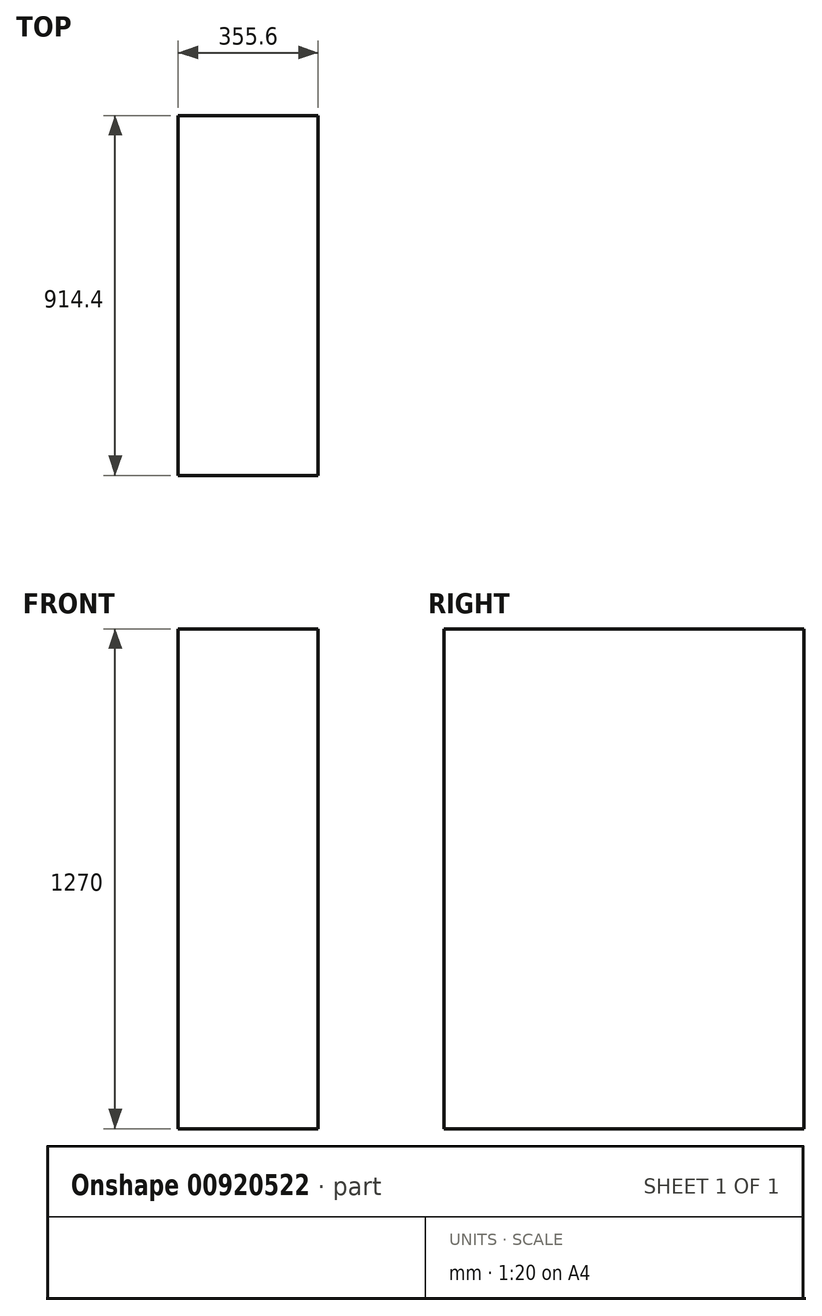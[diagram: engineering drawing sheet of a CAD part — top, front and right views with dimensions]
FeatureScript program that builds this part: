
annotation { "Feature Type Name" : "Feature", "Feature Type Description" : "" }
export const myFeature = defineFeature(function(context is Context, id is Id, definition is map)
    precondition{}
    {
        {
            var Q0;
            Q0=qCreatedBy(makeId("Top.planeOp"),FACE);
            var sketch = newSketch(context, id + "F0", { "sketchPlane" : qUnion([Q0])});
            skLineSegment(sketch, "E0.bottom", {"start": v(177.8, -457.2) * mm, "end": v(-177.8, -457.2) * mm});
            skLineSegment(sketch, "E0.top", {"start": v(177.8, 457.2) * mm, "end": v(-177.8, 457.2) * mm});
            skLineSegment(sketch, "E0.left", {"start": v(177.8, -457.2) * mm, "end": v(177.8, 457.2) * mm});
            skLineSegment(sketch, "E0.right", {"start": v(-177.8, -457.2) * mm, "end": v(-177.8, 457.2) * mm});
            skPoint(sketch, "E0.middle", {"position": v(0, 0) * mm});
            skSolve(sketch);
        }
        {
            var Q0;
            Q0 = qSketchRegion(id + "F0", true);
            extrude(context, id + "F1", {"entities" : qUnion([Q0]), "depth" : 1270 * mm, "offsetDistance" : 25.4 * mm});
        }
    });
